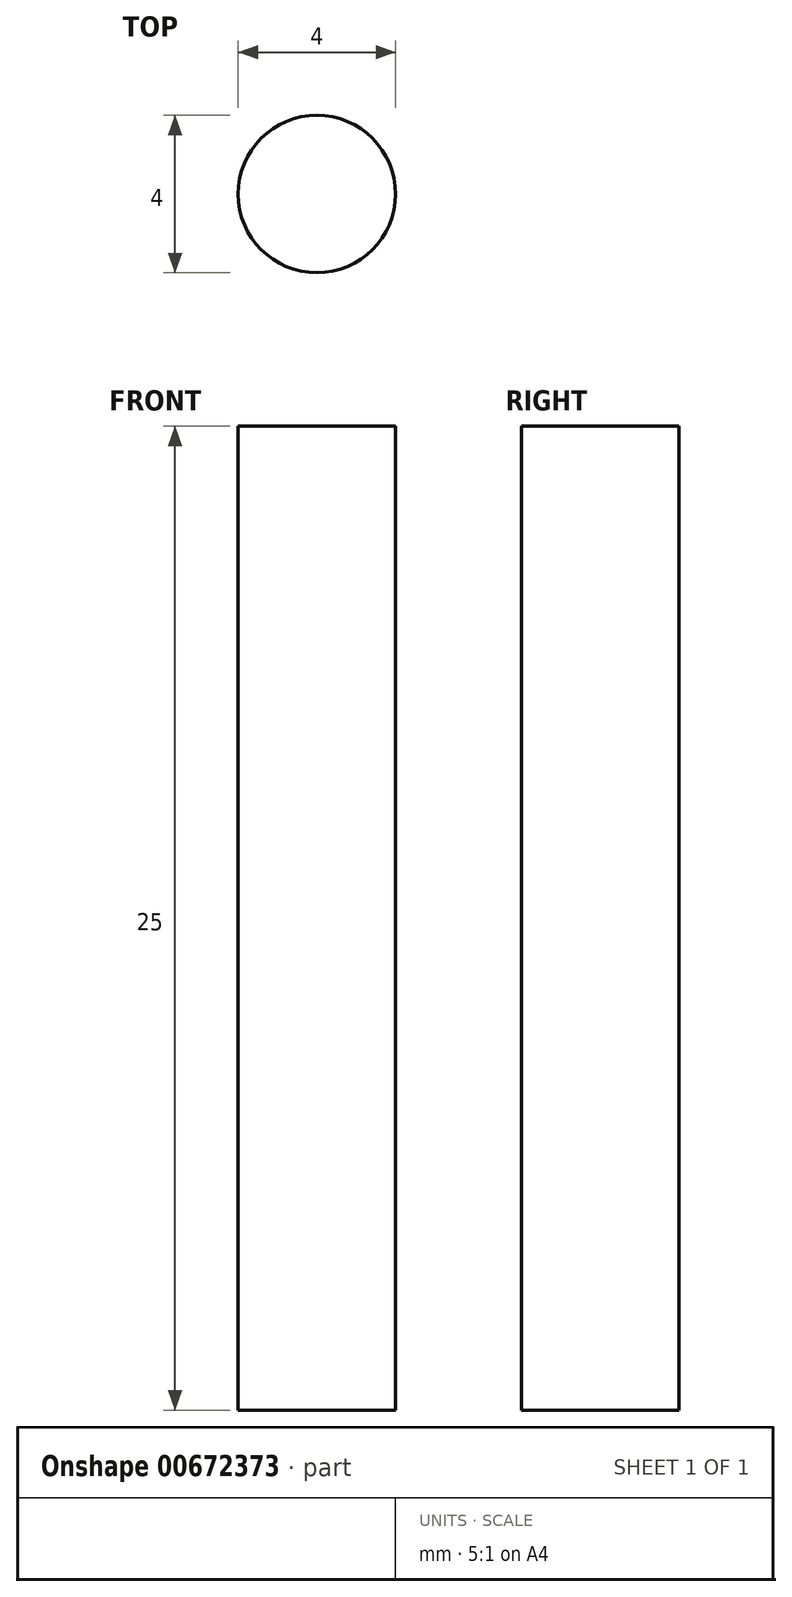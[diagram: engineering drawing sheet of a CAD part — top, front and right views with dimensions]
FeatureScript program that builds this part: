
annotation { "Feature Type Name" : "Feature", "Feature Type Description" : "" }
export const myFeature = defineFeature(function(context is Context, id is Id, definition is map)
    precondition{}
    {
        {
            var Q0;
            Q0=qCreatedBy(makeId("Top.planeOp"),FACE);
            var sketch = newSketch(context, id + "F0", { "sketchPlane" : qUnion([Q0])});
            skCircle(sketch, "E0", {"center": v(0, 0) * mm, "radius": 2 * mm});
            skSolve(sketch);
        }
        {
            var Q0;
            Q0 = qSketchRegion(id + "F0", true);
            extrude(context, id + "F1", {"entities" : qUnion([Q0]), "depth" : 25 * mm, "offsetDistance" : 25 * mm});
        }
    });
